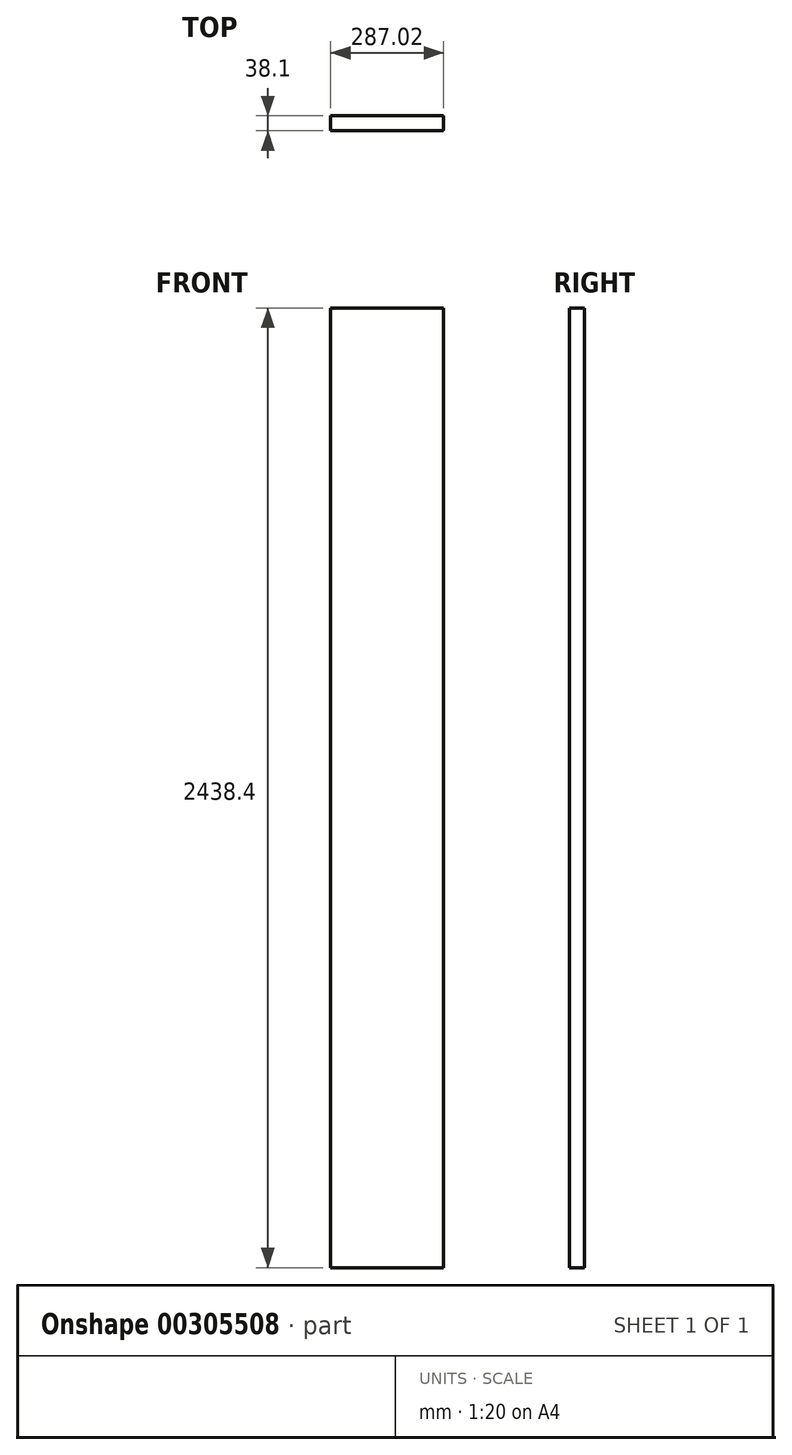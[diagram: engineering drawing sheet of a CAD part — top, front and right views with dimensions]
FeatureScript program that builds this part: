
annotation { "Feature Type Name" : "Feature", "Feature Type Description" : "" }
export const myFeature = defineFeature(function(context is Context, id is Id, definition is map)
    precondition{}
    {
        {
            var Q0;
            Q0=qCreatedBy(makeId("Top.planeOp"),FACE);
            var sketch = newSketch(context, id + "F0", { "sketchPlane" : qUnion([Q0])});
            skLineSegment(sketch, "E0.bottom", {"start": v(-144.97, 20.82) * mm, "end": v(142.05, 20.82) * mm});
            skLineSegment(sketch, "E0.top", {"start": v(-144.97, -17.28) * mm, "end": v(142.05, -17.28) * mm});
            skLineSegment(sketch, "E0.left", {"start": v(-144.97, 20.82) * mm, "end": v(-144.97, -17.28) * mm});
            skLineSegment(sketch, "E0.right", {"start": v(142.05, 20.82) * mm, "end": v(142.05, -17.28) * mm});
            skSolve(sketch);
        }
        {
            var Q0;
            Q0=makeQuery(id+"F0.imprint","IMPRINT",FACE,{"disambiguationData":[TD([[makeQuery(id+"F0.imprint","IMPRINT",EDGE,{"derivedFrom":sQuery(id+"F0.wireOp",EDGE,"E0.bottom")}),-1.0]])]});
            extrude(context, id + "F1", {"entities" : qUnion([Q0]), "depth" : 2438.4 * mm});
        }
    });
